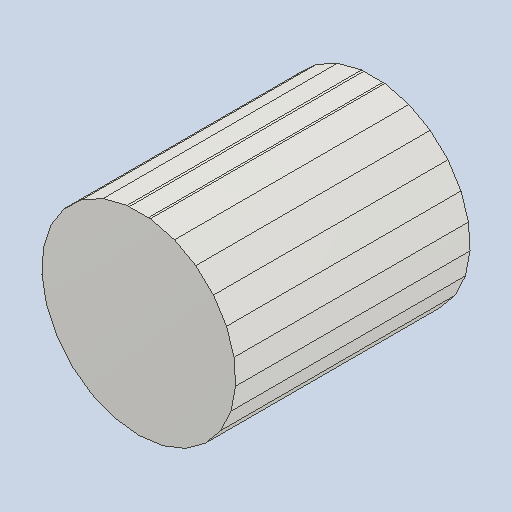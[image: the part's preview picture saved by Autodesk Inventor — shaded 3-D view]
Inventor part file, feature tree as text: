
AUTODESK INVENTOR PART (.ipt)
format: ipt  version: 2024 (Build 280153000, 153)  size: 151,552 bytes
history: native  units: mm (DEFAULTED — no unit token found)
features: other x3, extrude x2, fillet x1, pattern_circular x1
ambient origin geometry x8: Origin, YZ Plane, XZ Plane, XY Plane, X Axis, Y Axis, Z Axis, Center Point
bodies: Solid1 (feature_tree)
feature tree (7):
  other  "Pulley Sketch"
  extrude  "Base Body"  Depth=19.894368mm
  extrude  "Tooth"  Depth=0.3mm
  fillet  "Tooth Fillet"  Radius=2.67mm
  pattern_circular  "Teeth"  [2 undecoded]
  other  "Left flange"
  other  "Right flange"
note: 2 required parameter values undecoded (feature->parameter linkage not recoverable at this tier; creation-order binding heuristic only, values carry confidence <= 0.55)
